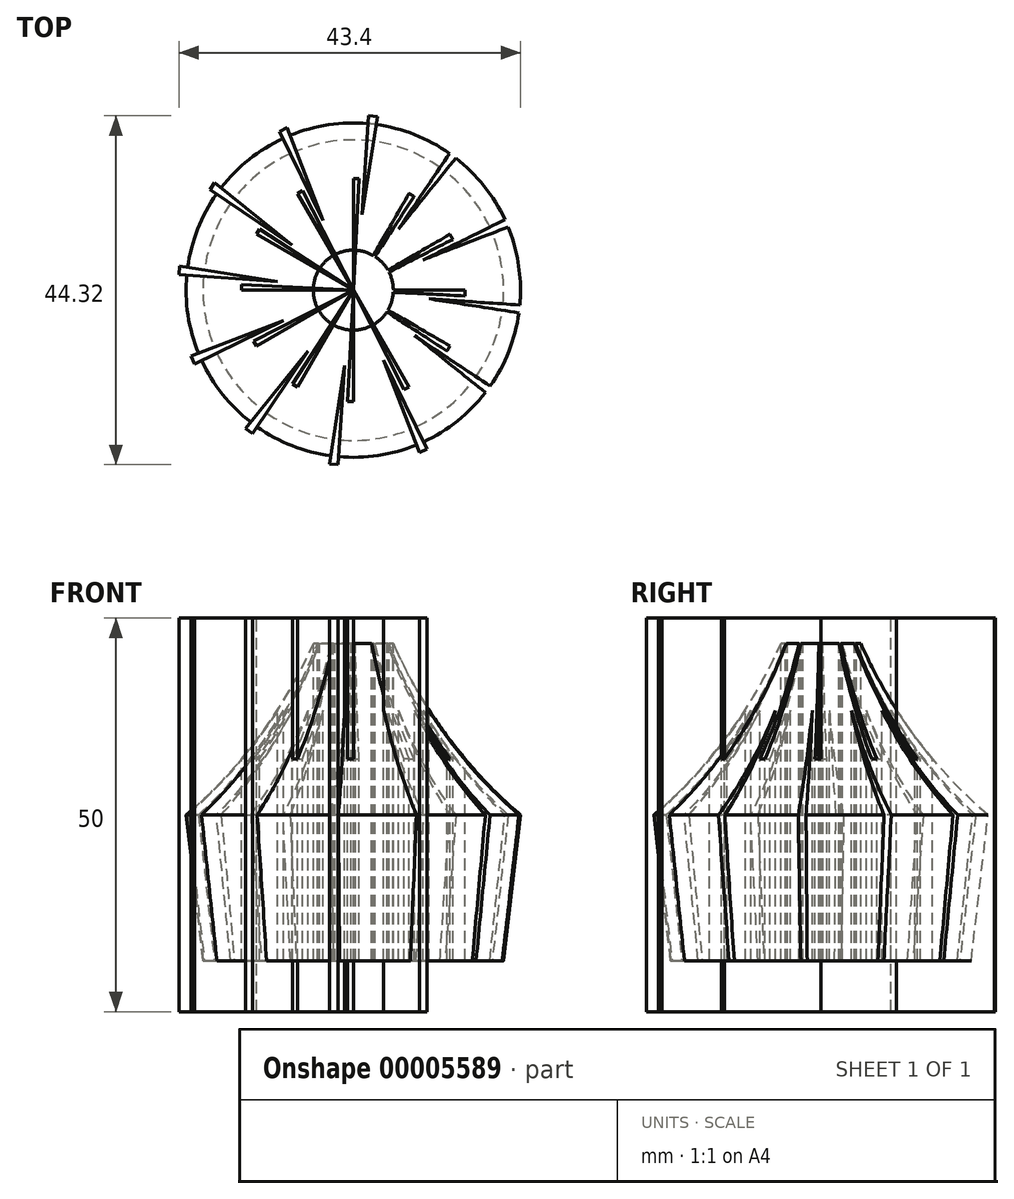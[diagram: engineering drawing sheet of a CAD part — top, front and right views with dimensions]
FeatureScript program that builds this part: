
annotation { "Feature Type Name" : "Feature", "Feature Type Description" : "" }
export const myFeature = defineFeature(function(context is Context, id is Id, definition is map)
    precondition{}
    {
        {
            var Q0;
            Q0=qCreatedBy(makeId("Right.planeOp"),FACE);
            var sketch = newSketch(context, id + "F0", { "sketchPlane" : qUnion([Q0])});
            skLineSegment(sketch, "E0", {"start": v(0, 48.43) * mm, "end": v(0, -18.54) * mm});
            skLineSegment(sketch, "E1", {"start": v(19.09, -18.54) * mm, "end": v(21.24, 0) * mm});
            skArc(sketch, "E2", {"start": v(0, 48.43) * mm, "mid": v(5.08, 21.79) * mm, "end": v(21.24, 0) * mm});
            skLineSegment(sketch, "E3", {"start": v(5.08, 21.79) * mm, "end": v(5.08, -18.54) * mm});
            skLineSegment(sketch, "E4", {"start": v(5.08, -18.54) * mm, "end": v(19.09, -18.54) * mm});
            skSolve(sketch);
        }
        {
            var Q0;
            {var subQ0=sQuery(id+"F0.wireOp",EDGE,"E1");Q0=makeQuery(id+"F0.imprint","IMPRINT",FACE,{"disambiguationData":[TD([[makeQuery(id+"F0.imprint","IMPRINT",EDGE,{"derivedFrom":subQ0}),1.0]])]});}
            var Q1;
            Q1=sQuery(id+"F0.wireOp",EDGE,"E0");
            revolve(context, id + "F1", {"entities" : qUnion([Q0]), "axis" : qUnion([Q1]), "revolveType" : RevolveType.FULL});
        }
        {
            var Q0;
            Q0=qCreatedBy(makeId("Top.planeOp"),FACE);
            var sketch = newSketch(context, id + "F2", { "sketchPlane" : qUnion([Q0])});
            skLineSegment(sketch, "E5", {"start": v(0, 0) * mm, "end": v(0, 14.18) * mm});
            skLineSegment(sketch, "E6", {"start": v(0, 14.18) * mm, "end": v(0.73, 14.18) * mm});
            skLineSegment(sketch, "E7", {"start": v(0.73, 14.18) * mm, "end": v(0, 0) * mm});
            skLineSegment(sketch, "E8", {"start": v(1.1, 9.6) * mm, "end": v(1.96, 22.16) * mm});
            skLineSegment(sketch, "E9", {"start": v(1.96, 22.16) * mm, "end": v(3.05, 22.07) * mm});
            skLineSegment(sketch, "E10", {"start": v(3.05, 22.07) * mm, "end": v(1.1, 9.6) * mm});
            skSolve(sketch);
        }
        {
            var Q0;
            Q0=makeQuery(id+"F2.imprint","IMPRINT",FACE,{"disambiguationData":[TD([[makeQuery(id+"F2.imprint","IMPRINT",EDGE,{"derivedFrom":sQuery(id+"F2.wireOp",EDGE,"E8")}),-1.0]])]});
            var Q1;
            Q1=makeQuery(id+"F2.imprint","IMPRINT",FACE,{"disambiguationData":[TD([[makeQuery(id+"F2.imprint","IMPRINT",EDGE,{"derivedFrom":sQuery(id+"F2.wireOp",EDGE,"E5")}),-1.0]])]});
            extrude(context, id + "F3", {"entities" : qUnion([Q0, Q1]), "oppositeDirection" : true, "depth" : 25 * mm, "hasSecondDirection" : true, "secondDirectionOppositeDirection" : false, "secondDirectionDepth" : 25 * mm});
        }
        {
            var Q0;
            Q0=makeQuery(id+"F3.opExtrude","SWEPT_BODY",BODY,{"disambiguationData":[OSD([sQuery(id+"F2.wireOp",EDGE,"E8"),sQuery(id+"F2.wireOp",EDGE,"E9"),sQuery(id+"F2.wireOp",EDGE,"E10")])]});
            var Q1;
            Q1=makeQuery(id+"F3.opExtrude","SWEPT_BODY",BODY,{"disambiguationData":[OSD([sQuery(id+"F2.wireOp",EDGE,"E5"),sQuery(id+"F2.wireOp",EDGE,"E6"),sQuery(id+"F2.wireOp",EDGE,"E7")])]});
            var Q2;
            Q2=makeQuery(id+"F3.opExtrude","SWEPT_EDGE",EDGE,{"disambiguationData":[OSD([sQuery(id+"F2.wireOp",EDGE,"E5"),sQuery(id+"F2.wireOp",EDGE,"E7")])]});
            circularPattern(context, id + "F4", {"entities" : qUnion([Q0, Q1]), "axis" : qUnion([Q2]), "angle" : 30 * degree, "instanceCount" : 20});
        }
        {
            var Q0;
            Q0=makeQuery(id+"F4.opPattern","COPY",BODY,{"derivedFrom":makeQuery(id+"F3.opExtrude","SWEPT_BODY",BODY,{"disambiguationData":[OSD([sQuery(id+"F2.wireOp",EDGE,"E8"),sQuery(id+"F2.wireOp",EDGE,"E9"),sQuery(id+"F2.wireOp",EDGE,"E10")])]}),"instanceName":"5"});
            var Q1;
            Q1=makeQuery(id+"F4.opPattern","COPY",BODY,{"derivedFrom":makeQuery(id+"F3.opExtrude","SWEPT_BODY",BODY,{"disambiguationData":[OSD([sQuery(id+"F2.wireOp",EDGE,"E8"),sQuery(id+"F2.wireOp",EDGE,"E9"),sQuery(id+"F2.wireOp",EDGE,"E10")])]}),"instanceName":"18"});
            var Q2;
            Q2=makeQuery(id+"F4.opPattern","COPY",BODY,{"derivedFrom":makeQuery(id+"F3.opExtrude","SWEPT_BODY",BODY,{"disambiguationData":[OSD([sQuery(id+"F2.wireOp",EDGE,"E8"),sQuery(id+"F2.wireOp",EDGE,"E9"),sQuery(id+"F2.wireOp",EDGE,"E10")])]}),"instanceName":"4"});
            var Q3;
            Q3=makeQuery(id+"F4.opPattern","COPY",BODY,{"derivedFrom":makeQuery(id+"F3.opExtrude","SWEPT_BODY",BODY,{"disambiguationData":[OSD([sQuery(id+"F2.wireOp",EDGE,"E8"),sQuery(id+"F2.wireOp",EDGE,"E9"),sQuery(id+"F2.wireOp",EDGE,"E10")])]}),"instanceName":"15"});
            var Q4;
            Q4=makeQuery(id+"F4.opPattern","COPY",BODY,{"derivedFrom":makeQuery(id+"F3.opExtrude","SWEPT_BODY",BODY,{"disambiguationData":[OSD([sQuery(id+"F2.wireOp",EDGE,"E8"),sQuery(id+"F2.wireOp",EDGE,"E9"),sQuery(id+"F2.wireOp",EDGE,"E10")])]}),"instanceName":"2"});
            var Q5;
            Q5=makeQuery(id+"F4.opPattern","COPY",BODY,{"derivedFrom":makeQuery(id+"F3.opExtrude","SWEPT_BODY",BODY,{"disambiguationData":[OSD([sQuery(id+"F2.wireOp",EDGE,"E8"),sQuery(id+"F2.wireOp",EDGE,"E9"),sQuery(id+"F2.wireOp",EDGE,"E10")])]}),"instanceName":"13"});
            var Q6;
            Q6=makeQuery(id+"F4.opPattern","COPY",BODY,{"derivedFrom":makeQuery(id+"F3.opExtrude","SWEPT_BODY",BODY,{"disambiguationData":[OSD([sQuery(id+"F2.wireOp",EDGE,"E8"),sQuery(id+"F2.wireOp",EDGE,"E9"),sQuery(id+"F2.wireOp",EDGE,"E10")])]}),"instanceName":"11"});
            var Q7;
            Q7=makeQuery(id+"F4.opPattern","COPY",BODY,{"derivedFrom":makeQuery(id+"F3.opExtrude","SWEPT_BODY",BODY,{"disambiguationData":[OSD([sQuery(id+"F2.wireOp",EDGE,"E8"),sQuery(id+"F2.wireOp",EDGE,"E9"),sQuery(id+"F2.wireOp",EDGE,"E10")])]}),"instanceName":"9"});
            var Q8;
            Q8=makeQuery(id+"F4.opPattern","COPY",BODY,{"derivedFrom":makeQuery(id+"F3.opExtrude","SWEPT_BODY",BODY,{"disambiguationData":[OSD([sQuery(id+"F2.wireOp",EDGE,"E8"),sQuery(id+"F2.wireOp",EDGE,"E9"),sQuery(id+"F2.wireOp",EDGE,"E10")])]}),"instanceName":"8"});
            var Q9;
            Q9=makeQuery(id+"F4.opPattern","COPY",BODY,{"derivedFrom":makeQuery(id+"F3.opExtrude","SWEPT_BODY",BODY,{"disambiguationData":[OSD([sQuery(id+"F2.wireOp",EDGE,"E5"),sQuery(id+"F2.wireOp",EDGE,"E6"),sQuery(id+"F2.wireOp",EDGE,"E7")])]}),"instanceName":"7"});
            var Q10;
            Q10=makeQuery(id+"F4.opPattern","COPY",BODY,{"derivedFrom":makeQuery(id+"F3.opExtrude","SWEPT_BODY",BODY,{"disambiguationData":[OSD([sQuery(id+"F2.wireOp",EDGE,"E5"),sQuery(id+"F2.wireOp",EDGE,"E6"),sQuery(id+"F2.wireOp",EDGE,"E7")])]}),"instanceName":"6"});
            var Q11;
            Q11=makeQuery(id+"F4.opPattern","COPY",BODY,{"derivedFrom":makeQuery(id+"F3.opExtrude","SWEPT_BODY",BODY,{"disambiguationData":[OSD([sQuery(id+"F2.wireOp",EDGE,"E5"),sQuery(id+"F2.wireOp",EDGE,"E6"),sQuery(id+"F2.wireOp",EDGE,"E7")])]}),"instanceName":"17"});
            var Q12;
            Q12=makeQuery(id+"F4.opPattern","COPY",BODY,{"derivedFrom":makeQuery(id+"F3.opExtrude","SWEPT_BODY",BODY,{"disambiguationData":[OSD([sQuery(id+"F2.wireOp",EDGE,"E5"),sQuery(id+"F2.wireOp",EDGE,"E6"),sQuery(id+"F2.wireOp",EDGE,"E7")])]}),"instanceName":"4"});
            var Q13;
            Q13=makeQuery(id+"F4.opPattern","COPY",BODY,{"derivedFrom":makeQuery(id+"F3.opExtrude","SWEPT_BODY",BODY,{"disambiguationData":[OSD([sQuery(id+"F2.wireOp",EDGE,"E5"),sQuery(id+"F2.wireOp",EDGE,"E6"),sQuery(id+"F2.wireOp",EDGE,"E7")])]}),"instanceName":"3"});
            var Q14;
            Q14=makeQuery(id+"F4.opPattern","COPY",BODY,{"derivedFrom":makeQuery(id+"F3.opExtrude","SWEPT_BODY",BODY,{"disambiguationData":[OSD([sQuery(id+"F2.wireOp",EDGE,"E5"),sQuery(id+"F2.wireOp",EDGE,"E6"),sQuery(id+"F2.wireOp",EDGE,"E7")])]}),"instanceName":"14"});
            var Q15;
            Q15=makeQuery(id+"F4.opPattern","COPY",BODY,{"derivedFrom":makeQuery(id+"F3.opExtrude","SWEPT_BODY",BODY,{"disambiguationData":[OSD([sQuery(id+"F2.wireOp",EDGE,"E5"),sQuery(id+"F2.wireOp",EDGE,"E6"),sQuery(id+"F2.wireOp",EDGE,"E7")])]}),"instanceName":"1"});
            var Q16;
            Q16=makeQuery(id+"F3.opExtrude","SWEPT_BODY",BODY,{"disambiguationData":[OSD([sQuery(id+"F2.wireOp",EDGE,"E5"),sQuery(id+"F2.wireOp",EDGE,"E6"),sQuery(id+"F2.wireOp",EDGE,"E7")])]});
            var Q17;
            Q17=makeQuery(id+"F4.opPattern","COPY",BODY,{"derivedFrom":makeQuery(id+"F3.opExtrude","SWEPT_BODY",BODY,{"disambiguationData":[OSD([sQuery(id+"F2.wireOp",EDGE,"E5"),sQuery(id+"F2.wireOp",EDGE,"E6"),sQuery(id+"F2.wireOp",EDGE,"E7")])]}),"instanceName":"11"});
            var Q18;
            Q18=makeQuery(id+"F4.opPattern","COPY",BODY,{"derivedFrom":makeQuery(id+"F3.opExtrude","SWEPT_BODY",BODY,{"disambiguationData":[OSD([sQuery(id+"F2.wireOp",EDGE,"E5"),sQuery(id+"F2.wireOp",EDGE,"E6"),sQuery(id+"F2.wireOp",EDGE,"E7")])]}),"instanceName":"10"});
            var Q19;
            Q19=makeQuery(id+"F4.opPattern","COPY",BODY,{"derivedFrom":makeQuery(id+"F3.opExtrude","SWEPT_BODY",BODY,{"disambiguationData":[OSD([sQuery(id+"F2.wireOp",EDGE,"E8"),sQuery(id+"F2.wireOp",EDGE,"E9"),sQuery(id+"F2.wireOp",EDGE,"E10")])]}),"instanceName":"10"});
            var Q20;
            Q20=makeQuery(id+"F4.opPattern","COPY",BODY,{"derivedFrom":makeQuery(id+"F3.opExtrude","SWEPT_BODY",BODY,{"disambiguationData":[OSD([sQuery(id+"F2.wireOp",EDGE,"E5"),sQuery(id+"F2.wireOp",EDGE,"E6"),sQuery(id+"F2.wireOp",EDGE,"E7")])]}),"instanceName":"9"});
            var Q21;
            Q21=makeQuery(id+"F4.opPattern","COPY",BODY,{"derivedFrom":makeQuery(id+"F3.opExtrude","SWEPT_BODY",BODY,{"disambiguationData":[OSD([sQuery(id+"F2.wireOp",EDGE,"E8"),sQuery(id+"F2.wireOp",EDGE,"E9"),sQuery(id+"F2.wireOp",EDGE,"E10")])]}),"instanceName":"7"});
            var Q22;
            Q22=makeQuery(id+"F4.opPattern","COPY",BODY,{"derivedFrom":makeQuery(id+"F3.opExtrude","SWEPT_BODY",BODY,{"disambiguationData":[OSD([sQuery(id+"F2.wireOp",EDGE,"E5"),sQuery(id+"F2.wireOp",EDGE,"E6"),sQuery(id+"F2.wireOp",EDGE,"E7")])]}),"instanceName":"8"});
            var Q23;
            Q23=makeQuery(id+"F1.opRevolve","SWEPT_BODY",BODY,{"disambiguationData":[OSD([sQuery(id+"F0.wireOp",EDGE,"E1"),sQuery(id+"F0.wireOp",EDGE,"E2"),sQuery(id+"F0.wireOp",EDGE,"E3"),sQuery(id+"F0.wireOp",EDGE,"E4")])]});
            booleanBodies(context, id + "F5", {"operationType" : BooleanOperationType.SUBTRACTION, "tools" : qUnion([Q0, Q1, Q2, Q3, Q4, Q5, Q6, Q7, Q8, Q9, Q10, Q11, Q12, Q13, Q14, Q15, Q16, Q17, Q18, Q19, Q20, Q21, Q22]), "targets" : qUnion([Q23])});
        }
    });
